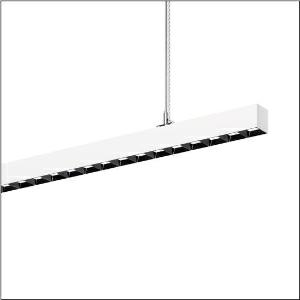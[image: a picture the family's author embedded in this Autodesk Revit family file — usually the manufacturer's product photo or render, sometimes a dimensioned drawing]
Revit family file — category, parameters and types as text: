
# Revit family: silica_r__21_51mx31dc4dwb_7dad
name_source: partatom
category: Lighting Fixtures
units: mm (PartAtom-declared; Revit-internal decimal feet)

## family parameters
Cut with Voids When Loaded = No
Host = Face
Light Source = No
Part Type = Normal
Room Calculation Point = No
Round Connector Dimension = Use Diameter
Shared = No

## types (1)
- --- (1 x LED, 18230 lm, 105.9 W, 4000K)
    Apparent Load = 106 VA
    CIE Flux Codes = 87 99 100 59 100
    Color Rendering = 80
    Color Temperature = 4000K
    Default Elevation = 1800 mm
    Description = Silica® 21, office luminaire, primary light control with darklight reflector, of PMMA, black, CAT 2 (L<= 3000cd/m²), light emission: direct/indirect distribution, primary light characteristic: symmetric, installation type: suspended mounting, LED, rated luminous flux: 18.230lm, luminous efficacy: 172lm/W, light colour: 840, colour temperature: 4000K, with terminal, 3+2-pole, max. 2.5mm², mains connection: 220..240V, AC, 50/60Hz, rated input power: 105.9W, luminaire housing, of aluminium, traffic white (RAL 9016), length: 3.004mm, width: 53mm, height: 53mm, protection rating (complete): IP20, insulation class (complete): insulation class I (protective earthing), certification: CE, permissible operating ambient temperature: 0..+35°C, standard: EN 50419, packaging unit: 1 piece
    Height = 53 mm
    Lamp = 1 x LED
    Lamp Light Flux = 18230 lm
    Lamp Power = 105.9 W
    Lamp count = 1
    Length = 3004 mm
    Luminous efficacy = 172 lm/W
    Manufacturer = Siteco
    ModVariant = No
    Model = 51MX31DC4DWB
    Mounting Place = Ceiling
    Mounting Type = Pendant
    Number of Poles = 1
    OnlyDefault = Yes
    Power Factor = 1
    Product Name = Silica® 21
    Product group = office luminaire | ceiling pendant
    ProductGroupID = 902
    Protection Class = Protection class I
    Protection Degree = IP 20
    RLX_Detail_Level = 1
    RLX_Emergency_Light_Flux = 0 lm
    RLX_Emergency_Type = 0
    RLX_Emergency_Type_DB = No
    RlxData = <blob elided: 64441 chars, md5=5636ce2f>
    Socket = socket
    Standby Power = 0 W
    System Light Flux = 18230 lm
    System Power = 106 W
    Type Comments = factory setting: luminous flux: 100 % | dim-lin: 254 | 367 mA
    Type Image = l_1335871.jpg
    URL = http://relux.com
    VarID = @adj_090731
    Voltage = 0 V
    Weight = 0.00 kg
    Width = 53 mm

## geometry (parser evidence)
native form markers: Blend x4, Sweep x11
no freeform markers — native parametric forms only
